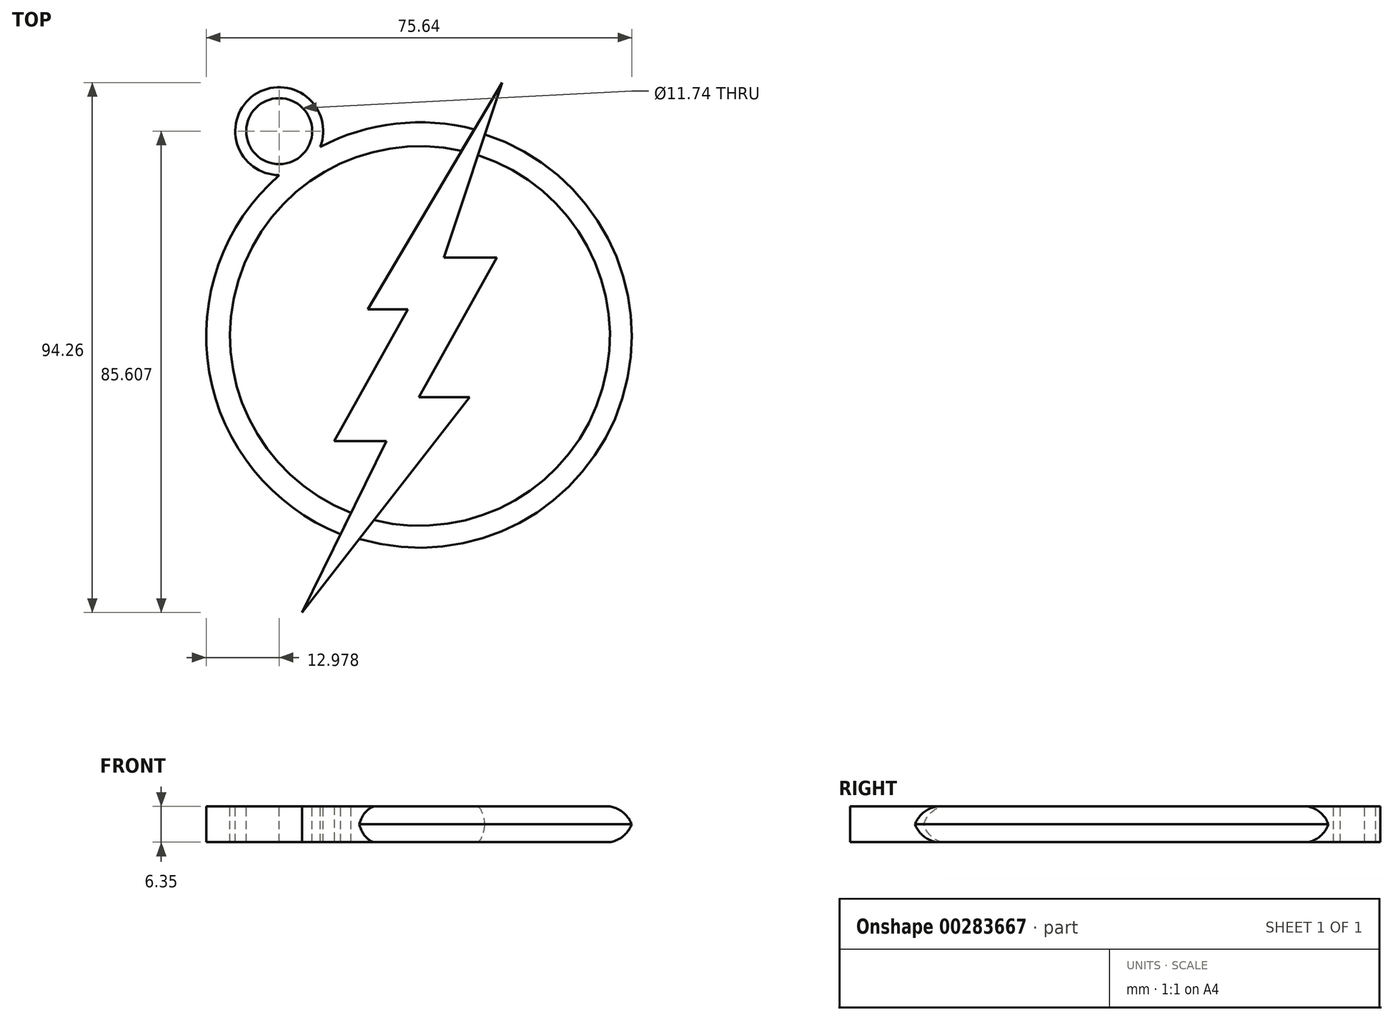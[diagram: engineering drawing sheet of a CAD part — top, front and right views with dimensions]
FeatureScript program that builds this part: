
annotation { "Feature Type Name" : "Feature", "Feature Type Description" : "" }
export const myFeature = defineFeature(function(context is Context, id is Id, definition is map)
    precondition{}
    {
        {
            var Q0;
            Q0=qCreatedBy(makeId("Top.planeOp"),FACE);
            var sketch = newSketch(context, id + "F0", { "sketchPlane" : qUnion([Q0])});
            skLineSegment(sketch, "E0", {"start": v(20.53, 51.39) * mm, "end": v(-3.33, 11.02) * mm});
            skLineSegment(sketch, "E1", {"start": v(-3.33, 11.02) * mm, "end": v(3.78, 11.02) * mm});
            skLineSegment(sketch, "E2", {"start": v(3.78, 11.02) * mm, "end": v(-9.3, -12.37) * mm});
            skLineSegment(sketch, "E3", {"start": v(-9.3, -12.37) * mm, "end": v(0, -12.37) * mm});
            skLineSegment(sketch, "E4", {"start": v(0, -12.37) * mm, "end": v(-15.02, -42.87) * mm});
            skLineSegment(sketch, "E5", {"start": v(-15.02, -42.87) * mm, "end": v(14.8, -4.57) * mm});
            skLineSegment(sketch, "E6", {"start": v(14.8, -4.57) * mm, "end": v(5.75, -4.57) * mm});
            skLineSegment(sketch, "E7", {"start": v(5.75, -4.57) * mm, "end": v(19.61, 20.24) * mm});
            skLineSegment(sketch, "E8", {"start": v(19.61, 20.24) * mm, "end": v(10.2, 20.24) * mm});
            skLineSegment(sketch, "E9", {"start": v(20.53, 51.39) * mm, "end": v(10.2, 20.24) * mm});
            skSolve(sketch);
        }
        {
            var Q0;
            Q0=qSketchRegion(id+"F0",true);
            extrude(context, id + "F1", {"entities" : qUnion([Q0]), "depth" : 6.35 * mm});
        }
        {
            var Q0;
            Q0=makeQuery(id+"F1.opExtrude","CAP_FACE",FACE,{"disambiguationData":[OSD([sQuery(id+"F0.wireOp",EDGE,"E0"),sQuery(id+"F0.wireOp",EDGE,"E1"),sQuery(id+"F0.wireOp",EDGE,"E2"),sQuery(id+"F0.wireOp",EDGE,"E3"),sQuery(id+"F0.wireOp",EDGE,"E4"),sQuery(id+"F0.wireOp",EDGE,"E5"),sQuery(id+"F0.wireOp",EDGE,"E6"),sQuery(id+"F0.wireOp",EDGE,"E7"),sQuery(id+"F0.wireOp",EDGE,"E8"),sQuery(id+"F0.wireOp",EDGE,"E9")])],"isStart":false});
            var sketch = newSketch(context, id + "F2", { "sketchPlane" : qUnion([Q0])});
            skCircle(sketch, "E10", {"center": v(5.95, 6.31) * mm, "radius": 33.75 * mm});
            skCircle(sketch, "E11", {"center": v(5.95, 6.31) * mm, "radius": 38 * mm});
            skSolve(sketch);
        }
        {
            var Q0;
            {var subQ0=sQuery(id+"F2.wireOp",EDGE,"E10");var subQ1=makeQuery(id+"F1.opExtrude","CAP_EDGE",EDGE,{"disambiguationData":[OSD([sQuery(id+"F0.wireOp",EDGE,"E0")])],"isStart":false});var subQ2=makeQuery(id+"F2.imprint","INTERSECT",VERTEX,{"derivedFrom":[subQ1,subQ0]});Q0=makeQuery(id+"F2.imprint","IMPRINT",FACE,{"disambiguationData":[TD([[makeQuery(id+"F2.imprint","IMPRINT",EDGE,{"disambiguationData":[TD([[subQ2,-1.0]])],"derivedFrom":subQ0}),-1.0]])]});}
            var Q1;
            {var subQ0=sQuery(id+"F2.wireOp",EDGE,"E10");var subQ1=makeQuery(id+"F1.opExtrude","CAP_EDGE",EDGE,{"disambiguationData":[OSD([sQuery(id+"F0.wireOp",EDGE,"E9")])],"isStart":false});var subQ2=makeQuery(id+"F2.imprint","INTERSECT",VERTEX,{"derivedFrom":[subQ1,subQ0]});Q1=makeQuery(id+"F2.imprint","IMPRINT",FACE,{"disambiguationData":[TD([[makeQuery(id+"F2.imprint","IMPRINT",EDGE,{"disambiguationData":[TD([[subQ2,1.0]])],"derivedFrom":subQ0}),-1.0]])]});}
            extrude(context, id + "F3", {"entities" : qUnion([Q0, Q1]), "oppositeDirection" : true, "depth" : 6.35 * mm});
        }
        {
            var Q0;
            Q0=makeQuery(id+"F1.opExtrude","CAP_FACE",FACE,{"disambiguationData":[OSD([sQuery(id+"F0.wireOp",EDGE,"E0"),sQuery(id+"F0.wireOp",EDGE,"E1"),sQuery(id+"F0.wireOp",EDGE,"E2"),sQuery(id+"F0.wireOp",EDGE,"E3"),sQuery(id+"F0.wireOp",EDGE,"E4"),sQuery(id+"F0.wireOp",EDGE,"E5"),sQuery(id+"F0.wireOp",EDGE,"E6"),sQuery(id+"F0.wireOp",EDGE,"E7"),sQuery(id+"F0.wireOp",EDGE,"E8"),sQuery(id+"F0.wireOp",EDGE,"E9")])],"isStart":false});
            var sketch = newSketch(context, id + "F4", { "sketchPlane" : qUnion([Q0])});
            skCircle(sketch, "E12", {"center": v(-19.06, 42.74) * mm, "radius": 7.82 * mm});
            skCircle(sketch, "E13", {"center": v(-19.06, 42.74) * mm, "radius": 5.87 * mm});
            skSolve(sketch);
        }
        {
            var Q0;
            Q0=qSketchRegion(id+"F4",true);
            extrude(context, id + "F5", {"entities" : qUnion([Q0]), "operationType" : NewBodyOperationType.ADD, "oppositeDirection" : true, "depth" : 6.35 * mm});
        }
        {
            var Q0;
            {var subQ0=sQuery(id+"F2.wireOp",EDGE,"E11");Q0=makeQuery(id+"F3.opExtrude","CAP_EDGE",EDGE,{"disambiguationData":[OSD([subQ0]),TDD([makeQuery(id+"F2.imprint","IMPRINT",EDGE,{"disambiguationData":[TD([[makeQuery(id+"F2.imprint","INTERSECT",VERTEX,{"derivedFrom":[makeQuery(id+"F1.opExtrude","CAP_EDGE",EDGE,{"disambiguationData":[OSD([sQuery(id+"F0.wireOp",EDGE,"E9")])],"isStart":false}),subQ0]}),1.0]])],"derivedFrom":subQ0})])],"isStart":true});}
            var Q1;
            {var subQ0=sQuery(id+"F2.wireOp",EDGE,"E11");Q1=makeQuery(id+"F3.opExtrude","CAP_EDGE",EDGE,{"disambiguationData":[OSD([subQ0]),TDD([makeQuery(id+"F2.imprint","IMPRINT",EDGE,{"disambiguationData":[TD([[makeQuery(id+"F2.imprint","INTERSECT",VERTEX,{"derivedFrom":[makeQuery(id+"F1.opExtrude","CAP_EDGE",EDGE,{"disambiguationData":[OSD([sQuery(id+"F0.wireOp",EDGE,"E9")])],"isStart":false}),subQ0]}),1.0]])],"derivedFrom":subQ0})])],"isStart":false});}
            fillet(context, id + "F6", {"entities" : qUnion([Q0, Q1]), "radius" : 5.08 * mm, "tangentPropagation" : true, "allowEdgeOverflow" : false});
        }
    });
